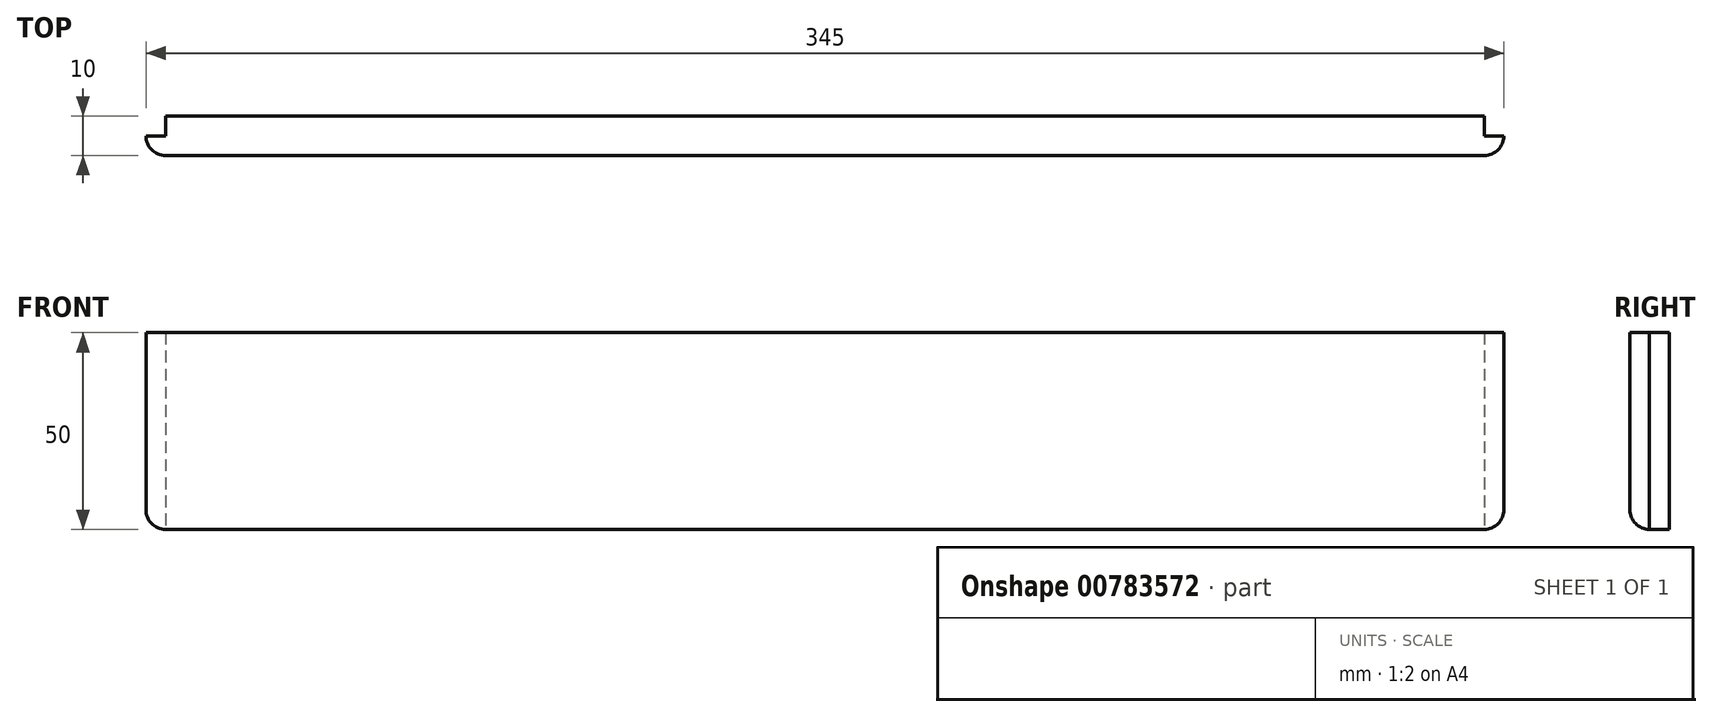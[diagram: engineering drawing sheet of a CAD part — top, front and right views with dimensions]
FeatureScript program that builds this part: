
annotation { "Feature Type Name" : "Feature", "Feature Type Description" : "" }
export const myFeature = defineFeature(function(context is Context, id is Id, definition is map)
    precondition{}
    {
        {
            var Q0;
            Q0=qCreatedBy(makeId("Front.planeOp"),FACE);
            var sketch = newSketch(context, id + "F0", { "sketchPlane" : qUnion([Q0])});
            skLineSegment(sketch, "E0.bottom", {"start": v(-171.82, 0) * mm, "end": v(173.18, 0) * mm});
            skLineSegment(sketch, "E0.top", {"start": v(-171.82, 25) * mm, "end": v(173.18, 25) * mm});
            skLineSegment(sketch, "E0.left", {"start": v(-171.82, 0) * mm, "end": v(-171.82, 25) * mm});
            skLineSegment(sketch, "E0.right", {"start": v(173.18, 0) * mm, "end": v(173.18, 25) * mm});
            skLineSegment(sketch, "E1.MirrorCS", {"start": v(-171.82, 0) * mm, "end": v(-171.82, -25) * mm});
            skLineSegment(sketch, "E2.MirrorCS", {"start": v(-171.82, -25) * mm, "end": v(173.18, -25) * mm});
            skLineSegment(sketch, "E3.MirrorCS", {"start": v(173.18, 0) * mm, "end": v(173.18, -25) * mm});
            skLineSegment(sketch, "E4", {"start": v(-171.82, 25) * mm, "end": v(-166.82, 25) * mm});
            skLineSegment(sketch, "E5", {"start": v(173.18, -25) * mm, "end": v(168.18, -25) * mm});
            skLineSegment(sketch, "E6.bottom", {"start": v(-166.82, 25) * mm, "end": v(168.18, 25) * mm});
            skLineSegment(sketch, "E6.top", {"start": v(-166.82, -25) * mm, "end": v(168.18, -25) * mm});
            skLineSegment(sketch, "E6.left", {"start": v(-166.82, 25) * mm, "end": v(-166.82, -25) * mm});
            skLineSegment(sketch, "E6.right", {"start": v(168.18, 25) * mm, "end": v(168.18, -25) * mm});
            skSolve(sketch);
        }
        {
            var Q0;
            {var subQ3=sQuery(id+"F0.wireOp",EDGE,"E0.left");Q0=makeQuery(id+"F0.imprint","IMPRINT",FACE,{"disambiguationData":[TD([[makeQuery(id+"F0.imprint","IMPRINT",EDGE,{"derivedFrom":subQ3}),-1.0]])]});}
            var Q1;
            {var subQ3=sQuery(id+"F0.wireOp",EDGE,"E1.MirrorCS");Q1=makeQuery(id+"F0.imprint","IMPRINT",FACE,{"disambiguationData":[TD([[makeQuery(id+"F0.imprint","IMPRINT",EDGE,{"derivedFrom":subQ3}),1.0]])]});}
            var Q2;
            {var subQ0=sQuery(id+"F0.wireOp",EDGE,"E6.left");var subQ1=sQuery(id+"F0.wireOp",EDGE,"E0.bottom");var subQ2=makeQuery(id+"F0.imprint","INTERSECT",VERTEX,{"derivedFrom":[subQ1,subQ0]});Q2=makeQuery(id+"F0.imprint","IMPRINT",FACE,{"disambiguationData":[TD([[makeQuery(id+"F0.imprint","IMPRINT",EDGE,{"disambiguationData":[TD([[subQ2,-1.0]])],"derivedFrom":subQ1}),-1.0]])]});}
            var Q3;
            {var subQ0=sQuery(id+"F0.wireOp",EDGE,"E6.left");var subQ1=sQuery(id+"F0.wireOp",EDGE,"E0.bottom");var subQ2=makeQuery(id+"F0.imprint","INTERSECT",VERTEX,{"derivedFrom":[subQ1,subQ0]});Q3=makeQuery(id+"F0.imprint","IMPRINT",FACE,{"disambiguationData":[TD([[makeQuery(id+"F0.imprint","IMPRINT",EDGE,{"disambiguationData":[TD([[subQ2,-1.0]])],"derivedFrom":subQ1}),1.0]])]});}
            var Q4;
            {var subQ0=sQuery(id+"F0.wireOp",EDGE,"E3.MirrorCS");Q4=makeQuery(id+"F0.imprint","IMPRINT",FACE,{"disambiguationData":[TD([[makeQuery(id+"F0.imprint","IMPRINT",EDGE,{"derivedFrom":subQ0}),-1.0]])]});}
            var Q5;
            {var subQ0=sQuery(id+"F0.wireOp",EDGE,"E0.right");Q5=makeQuery(id+"F0.imprint","IMPRINT",FACE,{"disambiguationData":[TD([[makeQuery(id+"F0.imprint","IMPRINT",EDGE,{"derivedFrom":subQ0}),1.0]])]});}
            extrude(context, id + "F1", {"entities" : qUnion([Q0, Q1, Q2, Q3, Q4, Q5]), "depth" : 5 * mm, "offsetDistance" : 25 * mm});
        }
        {
            var Q0;
            {var subQ0=sQuery(id+"F0.wireOp",EDGE,"E6.left");var subQ1=sQuery(id+"F0.wireOp",EDGE,"E0.bottom");var subQ2=makeQuery(id+"F0.imprint","INTERSECT",VERTEX,{"derivedFrom":[subQ1,subQ0]});Q0=makeQuery(id+"F0.imprint","IMPRINT",FACE,{"disambiguationData":[TD([[makeQuery(id+"F0.imprint","IMPRINT",EDGE,{"disambiguationData":[TD([[subQ2,-1.0]])],"derivedFrom":subQ1}),1.0]])]});}
            var Q1;
            {var subQ0=sQuery(id+"F0.wireOp",EDGE,"E6.left");var subQ1=sQuery(id+"F0.wireOp",EDGE,"E0.bottom");var subQ2=makeQuery(id+"F0.imprint","INTERSECT",VERTEX,{"derivedFrom":[subQ1,subQ0]});Q1=makeQuery(id+"F0.imprint","IMPRINT",FACE,{"disambiguationData":[TD([[makeQuery(id+"F0.imprint","IMPRINT",EDGE,{"disambiguationData":[TD([[subQ2,-1.0]])],"derivedFrom":subQ1}),-1.0]])]});}
            extrude(context, id + "F2", {"entities" : qUnion([Q0, Q1]), "operationType" : NewBodyOperationType.ADD, "depth" : 5 * mm, "offsetDistance" : 25 * mm});
        }
        {
            var Q0;
            {var subQ0=sQuery(id+"F0.wireOp",EDGE,"E6.left");var subQ1=sQuery(id+"F0.wireOp",EDGE,"E0.bottom");var subQ2=makeQuery(id+"F0.imprint","INTERSECT",VERTEX,{"derivedFrom":[subQ1,subQ0]});Q0=makeQuery(id+"F0.imprint","IMPRINT",FACE,{"disambiguationData":[TD([[makeQuery(id+"F0.imprint","IMPRINT",EDGE,{"disambiguationData":[TD([[subQ2,-1.0]])],"derivedFrom":subQ1}),1.0]])]});}
            var Q1;
            {var subQ0=sQuery(id+"F0.wireOp",EDGE,"E6.left");var subQ1=sQuery(id+"F0.wireOp",EDGE,"E0.bottom");var subQ2=makeQuery(id+"F0.imprint","INTERSECT",VERTEX,{"derivedFrom":[subQ1,subQ0]});Q1=makeQuery(id+"F0.imprint","IMPRINT",FACE,{"disambiguationData":[TD([[makeQuery(id+"F0.imprint","IMPRINT",EDGE,{"disambiguationData":[TD([[subQ2,-1.0]])],"derivedFrom":subQ1}),-1.0]])]});}
            extrude(context, id + "F3", {"entities" : qUnion([Q0, Q1]), "operationType" : NewBodyOperationType.ADD, "depth" : -5 * mm, "offsetDistance" : 25 * mm});
        }
        {
            var Q0;
            Q0=makeQuery(id+"F1.opExtrude","CAP_EDGE",EDGE,{"disambiguationData":[OSD([sQuery(id+"F0.wireOp",EDGE,"E0.left"),sQuery(id+"F0.wireOp",EDGE,"E1.MirrorCS")])],"isStart":false});
            var Q1;
            Q1=makeQuery(id+"F1.opExtrude","CAP_EDGE",EDGE,{"disambiguationData":[OSD([sQuery(id+"F0.wireOp",EDGE,"E0.right"),sQuery(id+"F0.wireOp",EDGE,"E3.MirrorCS")])],"isStart":false});
            fillet(context, id + "F4", {"entities" : qUnion([Q0, Q1]), "radius" : 5 * mm, "tangentPropagation" : true, "allowEdgeOverflow" : false});
        }
        {
            var Q0;
            Q0=makeQuery(id+"F1.opExtrude","CAP_EDGE",EDGE,{"disambiguationData":[OSD([sQuery(id+"F0.wireOp",EDGE,"E2.MirrorCS")])],"isStart":false});
            fillet(context, id + "F5", {"entities" : qUnion([Q0]), "radius" : 5 * mm, "tangentPropagation" : true, "allowEdgeOverflow" : false});
        }
    });
